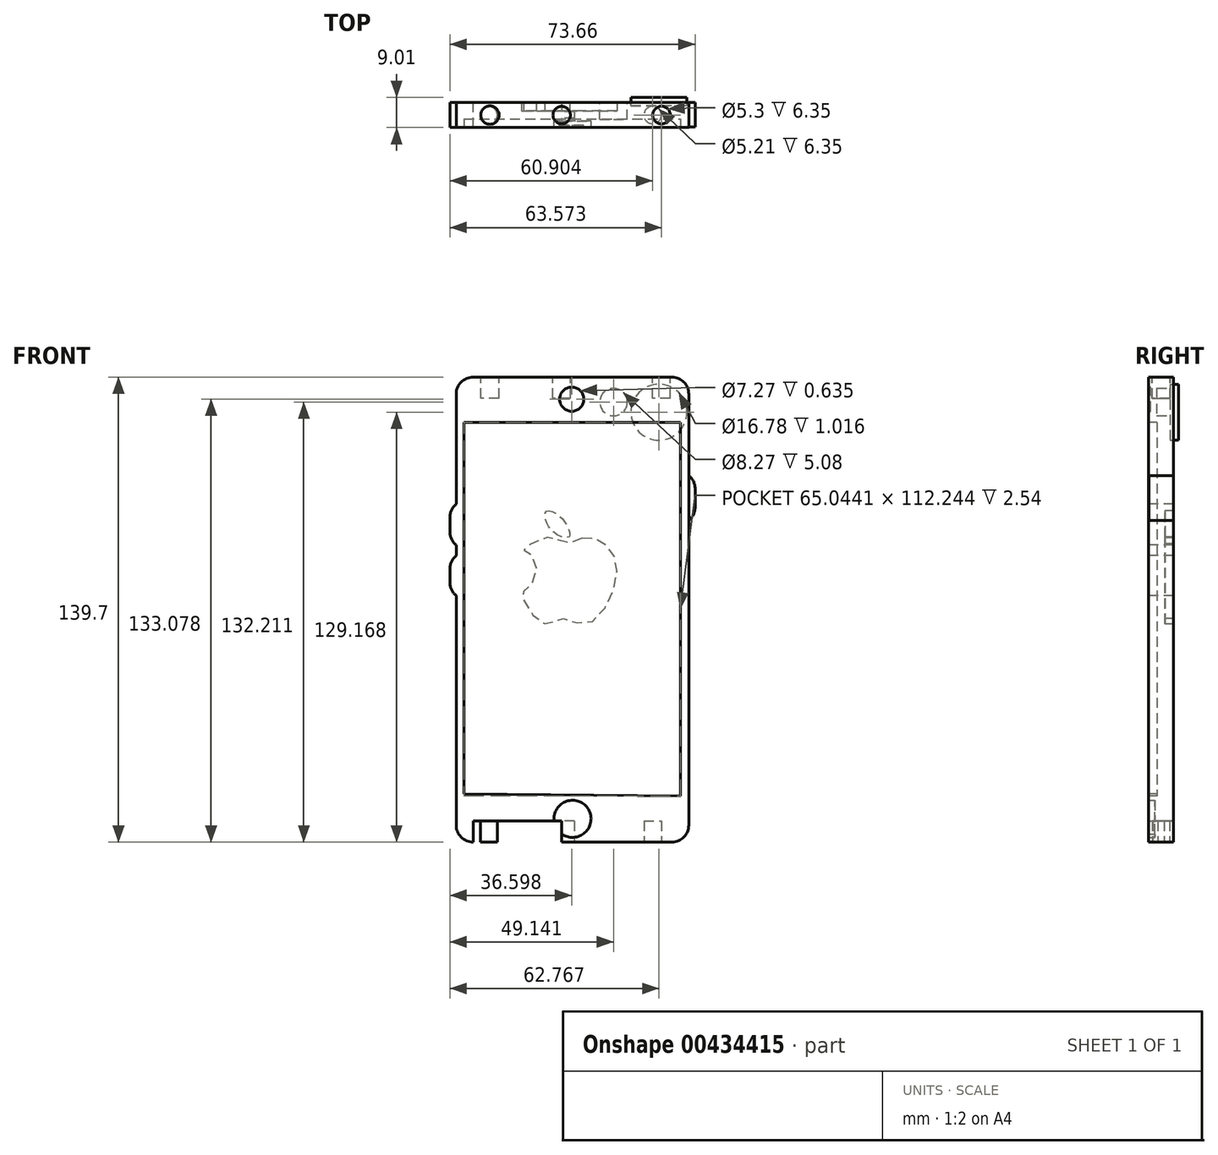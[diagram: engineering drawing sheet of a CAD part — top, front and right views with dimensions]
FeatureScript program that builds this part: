
annotation { "Feature Type Name" : "Feature", "Feature Type Description" : "" }
export const myFeature = defineFeature(function(context is Context, id is Id, definition is map)
    precondition{}
    {
        {
            var Q0;
            Q0=qCreatedBy(makeId("Front.planeOp"),FACE);
            var sketch = newSketch(context, id + "F0", { "sketchPlane" : qUnion([Q0])});
            skLineSegment(sketch, "E0.bottom", {"start": v(-31.68, 74.6) * mm, "end": v(38.17, 74.6) * mm});
            skLineSegment(sketch, "E0.top", {"start": v(-31.68, -65.1) * mm, "end": v(38.17, -65.1) * mm});
            skLineSegment(sketch, "E0.left", {"start": v(-31.68, 74.6) * mm, "end": v(-31.68, -65.1) * mm});
            skLineSegment(sketch, "E0.right", {"start": v(38.17, 74.6) * mm, "end": v(38.17, -65.1) * mm});
            skSolve(sketch);
        }
        {
            var Q0;
            Q0 = qSketchRegion(id + "F0", true);
            extrude(context, id + "F1", {"entities" : qUnion([Q0]), "depth" : 7.5 * mm});
        }
        {
            var Q0;
            Q0=makeQuery(id+"F1.opExtrude","SWEPT_EDGE",EDGE,{"disambiguationData":[OSD([sQuery(id+"F0.wireOp",EDGE,"E0.bottom"),sQuery(id+"F0.wireOp",EDGE,"E0.left")])]});
            var Q1;
            Q1=makeQuery(id+"F1.opExtrude","SWEPT_EDGE",EDGE,{"disambiguationData":[OSD([sQuery(id+"F0.wireOp",EDGE,"E0.bottom"),sQuery(id+"F0.wireOp",EDGE,"E0.right")])]});
            var Q2;
            Q2=makeQuery(id+"F1.opExtrude","SWEPT_EDGE",EDGE,{"disambiguationData":[OSD([sQuery(id+"F0.wireOp",EDGE,"E0.top"),sQuery(id+"F0.wireOp",EDGE,"E0.left")])]});
            var Q3;
            Q3=makeQuery(id+"F1.opExtrude","SWEPT_EDGE",EDGE,{"disambiguationData":[OSD([sQuery(id+"F0.wireOp",EDGE,"E0.top"),sQuery(id+"F0.wireOp",EDGE,"E0.right")])]});
            fillet(context, id + "F2", {"entities" : qUnion([Q0, Q1, Q2, Q3]), "radius" : 5.08 * mm, "tangentPropagation" : true, "allowEdgeOverflow" : false});
        }
        {
            var Q0;
            Q0=makeQuery(id+"F1.opExtrude","CAP_FACE",FACE,{"disambiguationData":[OSD([sQuery(id+"F0.wireOp",EDGE,"E0.bottom"),sQuery(id+"F0.wireOp",EDGE,"E0.top"),sQuery(id+"F0.wireOp",EDGE,"E0.left"),sQuery(id+"F0.wireOp",EDGE,"E0.right")])],"isStart":false});
            var sketch = newSketch(context, id + "F3", { "sketchPlane" : qUnion([Q0])});
            skLineSegment(sketch, "E1", {"start": v(-29.36, 61.01) * mm, "end": v(35.69, 61.01) * mm});
            skLineSegment(sketch, "E2", {"start": v(-29.36, 61.01) * mm, "end": v(-29.36, -50.65) * mm});
            skLineSegment(sketch, "E3", {"start": v(35.69, 61.01) * mm, "end": v(35.69, -51.23) * mm});
            skLineSegment(sketch, "E4", {"start": v(35.69, -51.23) * mm, "end": v(-29.36, -50.65) * mm});
            skSolve(sketch);
        }
        {
            var Q0;
            Q0 = qSketchRegion(id + "F3", true);
            extrude(context, id + "F4", {"entities" : qUnion([Q0]), "operationType" : NewBodyOperationType.REMOVE, "oppositeDirection" : true, "depth" : 2.54 * mm});
        }
        {
            var Q0;
            Q0=makeQuery(id+"F4.boolean.opBoolean","COPY",FACE,{"derivedFrom":makeQuery(id+"F4.opExtrude","CAP_FACE",FACE,{"disambiguationData":[OSD([sQuery(id+"F3.wireOp",EDGE,"E1"),sQuery(id+"F3.wireOp",EDGE,"E2"),sQuery(id+"F3.wireOp",EDGE,"E3"),sQuery(id+"F3.wireOp",EDGE,"E4")])],"isStart":false})});
            var sketch = newSketch(context, id + "F5", { "sketchPlane" : qUnion([Q0])});
            skSolve(sketch);
        }
        {
            var Q0;
            Q0 = qSketchRegion(id + "F5", true);
            var Q1;
            Q1=makeQuery(id+"F5.imprint","IMPRINT",FACE,{"disambiguationData":[TD([[makeQuery(id+"F5.imprint","IMPRINT",EDGE,{"derivedFrom":makeQuery(id+"F4.boolean.opBoolean","COPY",EDGE,{"derivedFrom":makeQuery(id+"F4.opExtrude","CAP_EDGE",EDGE,{"disambiguationData":[OSD([sQuery(id+"F3.wireOp",EDGE,"E1")])],"isStart":false})})}),-1.0]])]});
            extrude(context, id + "F6", {"entities" : qUnion([Q0, Q1]), "depth" : 2.54 * mm});
        }
        {
            var Q0;
            Q0=makeQuery(id+"F1.opExtrude","CAP_FACE",FACE,{"disambiguationData":[OSD([sQuery(id+"F0.wireOp",EDGE,"E0.bottom"),sQuery(id+"F0.wireOp",EDGE,"E0.top"),sQuery(id+"F0.wireOp",EDGE,"E0.left"),sQuery(id+"F0.wireOp",EDGE,"E0.right")])],"isStart":false});
            var sketch = newSketch(context, id + "F7", { "sketchPlane" : qUnion([Q0])});
            skCircle(sketch, "E5", {"center": v(3.24, -58.12) * mm, "radius": 5.57 * mm});
            skSolve(sketch);
        }
        {
            var Q0;
            Q0 = qSketchRegion(id + "F7", true);
            extrude(context, id + "F8", {"entities" : qUnion([Q0]), "operationType" : NewBodyOperationType.REMOVE, "oppositeDirection" : true, "depth" : 1.9 * mm});
        }
        {
            var Q0;
            Q0=makeQuery(id+"F8.boolean.opBoolean","COPY",FACE,{"derivedFrom":makeQuery(id+"F8.opExtrude","CAP_FACE",FACE,{"disambiguationData":[OSD([sQuery(id+"F7.wireOp",EDGE,"E5")])],"isStart":false})});
            var sketch = newSketch(context, id + "F9", { "sketchPlane" : qUnion([Q0])});
            skSolve(sketch);
        }
        {
            var Q0;
            Q0 = qSketchRegion(id + "F9", true);
            var Q1;
            Q1=makeQuery(id+"F9.imprint","IMPRINT",FACE,{"disambiguationData":[TD([[makeQuery(id+"F9.imprint","IMPRINT",EDGE,{"derivedFrom":makeQuery(id+"F8.boolean.opBoolean","COPY",EDGE,{"derivedFrom":makeQuery(id+"F8.opExtrude","CAP_EDGE",EDGE,{"disambiguationData":[OSD([sQuery(id+"F7.wireOp",EDGE,"E5")])],"isStart":false})})}),1.0]])]});
            extrude(context, id + "F10", {"entities" : qUnion([Q0, Q1]), "depth" : 1.9 * mm});
        }
        {
            var Q0;
            Q0=makeQuery(id+"F1.opExtrude","SWEPT_FACE",FACE,{"disambiguationData":[OSD([sQuery(id+"F0.wireOp",EDGE,"E0.bottom")])]});
            var sketch = newSketch(context, id + "F11", { "sketchPlane" : qUnion([Q0])});
            skCircle(sketch, "E6", {"center": v(0, -3.75) * mm, "radius": 2.63 * mm});
            skCircle(sketch, "E7", {"center": v(-21.56, -3.75) * mm, "radius": 2.75 * mm});
            skCircle(sketch, "E8", {"center": v(29.98, -3.75) * mm, "radius": 2.65 * mm});
            skPoint(sketch, "E9.orphan", {"position": v(-26.6, -3.75) * mm});
            skPoint(sketch, "E10.trimOffspring.end.orphan", {"position": v(33.09, -3.75) * mm});
            skPoint(sketch, "E11.orphan", {"position": v(0, -7.5) * mm});
            skPoint(sketch, "E12.start.orphan", {"position": v(0, 0) * mm});
            skSolve(sketch);
        }
        {
            var Q0;
            Q0 = qSketchRegion(id + "F11", true);
            extrude(context, id + "F12", {"entities" : qUnion([Q0]), "operationType" : NewBodyOperationType.REMOVE, "oppositeDirection" : true, "depth" : 6.35 * mm});
        }
        {
            var Q0;
            Q0=makeQuery(id+"F1.opExtrude","SWEPT_FACE",FACE,{"disambiguationData":[OSD([sQuery(id+"F0.wireOp",EDGE,"E0.top")])]});
            var sketch = newSketch(context, id + "F13", { "sketchPlane" : qUnion([Q0])});
            skLineSegment(sketch, "E13", {"start": v(0, 0) * mm, "end": v(0, 2.8) * mm});
            skLineSegment(sketch, "E14", {"start": v(-26.6, 3.75) * mm, "end": v(-3.81, 3.75) * mm});
            skLineSegment(sketch, "E15.bottom", {"start": v(3.81, 2.8) * mm, "end": v(-3.81, 2.8) * mm});
            skLineSegment(sketch, "E15.top", {"start": v(3.81, 4.7) * mm, "end": v(-3.81, 4.7) * mm});
            skLineSegment(sketch, "E15.left", {"start": v(3.8, 2.8) * mm, "end": v(3.8, 4.7) * mm});
            skLineSegment(sketch, "E15.right", {"start": v(-3.81, 2.8) * mm, "end": v(-3.81, 4.7) * mm});
            skPoint(sketch, "E15.middle", {"position": v(0, 3.75) * mm});
            skLineSegment(sketch, "E16.trimOffspring", {"start": v(3.81, 3.75) * mm, "end": v(33.09, 3.75) * mm});
            skLineSegment(sketch, "E17.trimOffspring", {"start": v(0, 4.7) * mm, "end": v(0, 7.5) * mm});
            skCircle(sketch, "E18", {"center": v(27.31, 3.75) * mm, "radius": 2.6 * mm});
            skCircle(sketch, "E19", {"center": v(-21.9, 3.75) * mm, "radius": 2.54 * mm});
            skSolve(sketch);
        }
        {
            var Q0;
            {var subQ6=sQuery(id+"F13.wireOp",EDGE,"E15.bottom");var subQ7=makeQuery(id+"F13.imprint","INTERSECT",VERTEX,{"derivedFrom":[sQuery(id+"F13.wireOp",EDGE,"E13"),subQ6]});Q0=makeQuery(id+"F13.imprint","IMPRINT",FACE,{"disambiguationData":[TD([[makeQuery(id+"F13.imprint","IMPRINT",EDGE,{"disambiguationData":[TD([[subQ7,1.0]])],"derivedFrom":subQ6}),-1.0]])]});}
            var Q1;
            {var subQ0=sQuery(id+"F13.wireOp",EDGE,"E19");var subQ1=sQuery(id+"F13.wireOp",EDGE,"E14");var subQ2=makeQuery(id+"F13.imprint","INTERSECT",VERTEX,{"disambiguationData":[OD(0.0)],"derivedFrom":[subQ1,subQ0]});Q1=makeQuery(id+"F13.imprint","IMPRINT",FACE,{"disambiguationData":[TD([[makeQuery(id+"F13.imprint","IMPRINT",EDGE,{"disambiguationData":[TD([[subQ2,-1.0]])],"derivedFrom":subQ1}),-1.0]])]});}
            var Q2;
            {var subQ0=sQuery(id+"F13.wireOp",EDGE,"E18");var subQ1=sQuery(id+"F13.wireOp",EDGE,"E16.trimOffspring");var subQ2=makeQuery(id+"F13.imprint","INTERSECT",VERTEX,{"disambiguationData":[OD(0.0)],"derivedFrom":[subQ1,subQ0]});Q2=makeQuery(id+"F13.imprint","IMPRINT",FACE,{"disambiguationData":[TD([[makeQuery(id+"F13.imprint","IMPRINT",EDGE,{"disambiguationData":[TD([[subQ2,-1.0]])],"derivedFrom":subQ1}),-1.0]])]});}
            var Q3;
            {var subQ0=sQuery(id+"F13.wireOp",EDGE,"E18");var subQ1=sQuery(id+"F13.wireOp",EDGE,"E16.trimOffspring");var subQ2=makeQuery(id+"F13.imprint","INTERSECT",VERTEX,{"disambiguationData":[OD(0.0)],"derivedFrom":[subQ1,subQ0]});Q3=makeQuery(id+"F13.imprint","IMPRINT",FACE,{"disambiguationData":[TD([[makeQuery(id+"F13.imprint","IMPRINT",EDGE,{"disambiguationData":[TD([[subQ2,-1.0]])],"derivedFrom":subQ1}),1.0]])]});}
            var Q4;
            {var subQ0=sQuery(id+"F13.wireOp",EDGE,"E19");var subQ1=sQuery(id+"F13.wireOp",EDGE,"E14");var subQ2=makeQuery(id+"F13.imprint","INTERSECT",VERTEX,{"disambiguationData":[OD(0.0)],"derivedFrom":[subQ1,subQ0]});Q4=makeQuery(id+"F13.imprint","IMPRINT",FACE,{"disambiguationData":[TD([[makeQuery(id+"F13.imprint","IMPRINT",EDGE,{"disambiguationData":[TD([[subQ2,-1.0]])],"derivedFrom":subQ1}),1.0]])]});}
            extrude(context, id + "F14", {"entities" : qUnion([Q0, Q1, Q2, Q3, Q4]), "operationType" : NewBodyOperationType.REMOVE, "oppositeDirection" : true, "depth" : 6.35 * mm});
        }
        {
            var Q0;
            Q0=makeQuery(id+"F1.opExtrude","CAP_FACE",FACE,{"disambiguationData":[OSD([sQuery(id+"F0.wireOp",EDGE,"E0.bottom"),sQuery(id+"F0.wireOp",EDGE,"E0.top"),sQuery(id+"F0.wireOp",EDGE,"E0.left"),sQuery(id+"F0.wireOp",EDGE,"E0.right")])],"isStart":false});
            var sketch = newSketch(context, id + "F15", { "sketchPlane" : qUnion([Q0])});
            skCircle(sketch, "E20", {"center": v(3, 67.98) * mm, "radius": 3.63 * mm});
            skSolve(sketch);
        }
        {
            var Q0;
            Q0 = qSketchRegion(id + "F15", true);
            extrude(context, id + "F16", {"entities" : qUnion([Q0]), "operationType" : NewBodyOperationType.REMOVE, "oppositeDirection" : true, "depth" : 0.64 * mm});
        }
        {
            var Q0;
            Q0=makeQuery(id+"F16.boolean.opBoolean","COPY",FACE,{"derivedFrom":makeQuery(id+"F16.opExtrude","CAP_FACE",FACE,{"disambiguationData":[OSD([sQuery(id+"F15.wireOp",EDGE,"E20")])],"isStart":false})});
            var sketch = newSketch(context, id + "F17", { "sketchPlane" : qUnion([Q0])});
            skSolve(sketch);
        }
        {
            var Q0;
            Q0 = qSketchRegion(id + "F17", true);
            var Q1;
            Q1=makeQuery(id+"F17.imprint","IMPRINT",FACE,{"disambiguationData":[TD([[makeQuery(id+"F17.imprint","IMPRINT",EDGE,{"derivedFrom":makeQuery(id+"F16.boolean.opBoolean","COPY",EDGE,{"derivedFrom":makeQuery(id+"F16.opExtrude","CAP_EDGE",EDGE,{"disambiguationData":[OSD([sQuery(id+"F15.wireOp",EDGE,"E20")])],"isStart":false})})}),1.0]])]});
            extrude(context, id + "F18", {"entities" : qUnion([Q0, Q1]), "depth" : 0.64 * mm});
        }
        {
            var Q0;
            Q0=makeQuery(id+"F1.opExtrude","SWEPT_FACE",FACE,{"disambiguationData":[OSD([sQuery(id+"F0.wireOp",EDGE,"E0.right")])]});
            var sketch = newSketch(context, id + "F19", { "sketchPlane" : qUnion([Q0])});
            skLineSegment(sketch, "E21.bottom", {"start": v(0, 31.58) * mm, "end": v(-7.37, 31.58) * mm});
            skLineSegment(sketch, "E21.top", {"start": v(0, 45.04) * mm, "end": v(-7.37, 45.04) * mm});
            skLineSegment(sketch, "E21.left", {"start": v(0, 31.58) * mm, "end": v(0, 45.04) * mm});
            skLineSegment(sketch, "E21.right", {"start": v(-7.37, 31.58) * mm, "end": v(-7.37, 45.04) * mm});
            skPoint(sketch, "E21.middle", {"position": v(-3.68, 38.31) * mm});
            skSolve(sketch);
        }
        {
            var Q0;
            Q0 = qSketchRegion(id + "F19", true);
            extrude(context, id + "F20", {"entities" : qUnion([Q0]), "operationType" : NewBodyOperationType.ADD, "depth" : 1.9 * mm});
        }
        {
            var Q0;
            Q0=makeQuery(id+"F20.opExtrude","CAP_EDGE",EDGE,{"disambiguationData":[OSD([sQuery(id+"F19.wireOp",EDGE,"E21.top")])],"isStart":false});
            var Q1;
            Q1=makeQuery(id+"F20.opExtrude","CAP_EDGE",EDGE,{"disambiguationData":[OSD([sQuery(id+"F19.wireOp",EDGE,"E21.bottom")])],"isStart":false});
            fillet(context, id + "F21", {"entities" : qUnion([Q0, Q1]), "radius" : 5.08 * mm, "tangentPropagation" : true, "allowEdgeOverflow" : false});
        }
        {
            var Q0;
            Q0=makeQuery(id+"F20.boolean.opBoolean","MERGE",FACE,{"derivedFrom":[makeQuery(id+"F1.opExtrude","CAP_FACE",FACE,{"disambiguationData":[OSD([sQuery(id+"F0.wireOp",EDGE,"E0.bottom"),sQuery(id+"F0.wireOp",EDGE,"E0.top"),sQuery(id+"F0.wireOp",EDGE,"E0.left"),sQuery(id+"F0.wireOp",EDGE,"E0.right")])],"isStart":true}),makeQuery(id+"F20.opExtrude","SWEPT_FACE",FACE,{"disambiguationData":[OSD([sQuery(id+"F19.wireOp",EDGE,"E21.left")])]})]});
            var sketch = newSketch(context, id + "F22", { "sketchPlane" : qUnion([Q0])});
            skCircle(sketch, "E22", {"center": v(-29.18, 64.07) * mm, "radius": 8.39 * mm});
            skSolve(sketch);
        }
        {
            var Q0;
            Q0 = qSketchRegion(id + "F22", true);
            extrude(context, id + "F23", {"entities" : qUnion([Q0]), "operationType" : NewBodyOperationType.REMOVE, "oppositeDirection" : true, "depth" : 1.02 * mm});
        }
        {
            var Q0;
            Q0=makeQuery(id+"F23.boolean.opBoolean","COPY",FACE,{"derivedFrom":makeQuery(id+"F23.opExtrude","CAP_FACE",FACE,{"disambiguationData":[OSD([sQuery(id+"F22.wireOp",EDGE,"E22")])],"isStart":false})});
            var sketch = newSketch(context, id + "F24", { "sketchPlane" : qUnion([Q0])});
            skSolve(sketch);
        }
        {
            var Q0;
            Q0=makeQuery(id+"F24.imprint","IMPRINT",FACE,{"disambiguationData":[TD([[makeQuery(id+"F24.imprint","IMPRINT",EDGE,{"derivedFrom":makeQuery(id+"F23.boolean.opBoolean","COPY",EDGE,{"derivedFrom":makeQuery(id+"F23.opExtrude","CAP_EDGE",EDGE,{"disambiguationData":[OSD([sQuery(id+"F22.wireOp",EDGE,"E22")])],"isStart":false})})}),1.0]])]});
            extrude(context, id + "F25", {"entities" : qUnion([Q0]), "depth" : 2.54 * mm});
        }
        {
            var Q0;
            Q0=makeQuery(id+"F20.boolean.opBoolean","MERGE",FACE,{"derivedFrom":[makeQuery(id+"F1.opExtrude","CAP_FACE",FACE,{"disambiguationData":[OSD([sQuery(id+"F0.wireOp",EDGE,"E0.bottom"),sQuery(id+"F0.wireOp",EDGE,"E0.top"),sQuery(id+"F0.wireOp",EDGE,"E0.left"),sQuery(id+"F0.wireOp",EDGE,"E0.right")])],"isStart":true}),makeQuery(id+"F20.opExtrude","SWEPT_FACE",FACE,{"disambiguationData":[OSD([sQuery(id+"F19.wireOp",EDGE,"E21.left")])]})]});
            var sketch = newSketch(context, id + "F26", { "sketchPlane" : qUnion([Q0])});
            skCircle(sketch, "E23", {"center": v(-15.55, 67.11) * mm, "radius": 4.13 * mm});
            skSolve(sketch);
        }
        {
            var Q0;
            Q0 = qSketchRegion(id + "F26", true);
            extrude(context, id + "F27", {"entities" : qUnion([Q0]), "operationType" : NewBodyOperationType.REMOVE, "oppositeDirection" : true, "depth" : 5.08 * mm});
        }
        {
            var Q0;
            Q0=makeQuery(id+"F27.boolean.opBoolean","COPY",FACE,{"derivedFrom":makeQuery(id+"F27.opExtrude","CAP_FACE",FACE,{"disambiguationData":[OSD([sQuery(id+"F26.wireOp",EDGE,"E23")])],"isStart":false})});
            var sketch = newSketch(context, id + "F28", { "sketchPlane" : qUnion([Q0])});
            skSolve(sketch);
        }
        {
            var Q0;
            Q0 = qSketchRegion(id + "F28", true);
            var Q1;
            Q1=makeQuery(id+"F28.imprint","IMPRINT",FACE,{"disambiguationData":[TD([[makeQuery(id+"F28.imprint","IMPRINT",EDGE,{"derivedFrom":makeQuery(id+"F27.boolean.opBoolean","COPY",EDGE,{"derivedFrom":makeQuery(id+"F27.opExtrude","CAP_EDGE",EDGE,{"disambiguationData":[OSD([sQuery(id+"F26.wireOp",EDGE,"E23")])],"isStart":false})})}),1.0]])]});
            extrude(context, id + "F29", {"entities" : qUnion([Q0, Q1]), "depth" : 5.08 * mm});
        }
        {
            var Q0;
            Q0=makeQuery(id+"F20.boolean.opBoolean","MERGE",FACE,{"derivedFrom":[makeQuery(id+"F1.opExtrude","CAP_FACE",FACE,{"disambiguationData":[OSD([sQuery(id+"F0.wireOp",EDGE,"E0.bottom"),sQuery(id+"F0.wireOp",EDGE,"E0.top"),sQuery(id+"F0.wireOp",EDGE,"E0.left"),sQuery(id+"F0.wireOp",EDGE,"E0.right")])],"isStart":true}),makeQuery(id+"F20.opExtrude","SWEPT_FACE",FACE,{"disambiguationData":[OSD([sQuery(id+"F19.wireOp",EDGE,"E21.left")])]})]});
            var sketch = newSketch(context, id + "F30", { "sketchPlane" : qUnion([Q0])});
            skFitSpline(sketch, "E24", {"points": [v(-6.1, 26.14) * mm, v(-1.6, 24.63) * mm, v(3.79, 26.54) * mm, v(11.48, 22.77) * mm, v(10.53, 22.5) * mm, v(7.66, 17.55) * mm, v(10.59, 10.58) * mm, v(12.05, 9.68) * mm, v(7.05, 1.53) * mm, v(3.17, 0.74) * mm, v(0, 2.1) * mm, v(-7.45, 0.52) * mm, v(-15.32, 10.02) * mm, v(-16, 20.24) * mm, v(-11.73, 25.3) * mm, v(-6.1, 26.14) * mm]});
            skFitSpline(sketch, "E25", {"points": [v(4.58, 34.28) * mm, v(0.67, 32.92) * mm, v(-2.35, 27.89) * mm, v(-2.11, 26.54) * mm, v(1.38, 27.24) * mm, v(4.75, 31.44) * mm, v(4.58, 34.28) * mm]});
            skSolve(sketch);
        }
        {
            var Q0;
            Q0=makeQuery(id+"F30.imprint","IMPRINT",FACE,{"disambiguationData":[TD([[makeQuery(id+"F30.imprint","IMPRINT",EDGE,{"derivedFrom":sQuery(id+"F30.wireOp",EDGE,"E25")}),1.0]])]});
            var sketch = newSketch(context, id + "F31", { "sketchPlane" : qUnion([Q0])});
            skSolve(sketch);
        }
        {
            var Q0;
            Q0=makeQuery(id+"F30.imprint","IMPRINT",FACE,{"disambiguationData":[TD([[makeQuery(id+"F30.imprint","IMPRINT",EDGE,{"derivedFrom":sQuery(id+"F30.wireOp",EDGE,"E24")}),-1.0]])]});
            extrude(context, id + "F32", {"entities" : qUnion([Q0]), "operationType" : NewBodyOperationType.REMOVE, "oppositeDirection" : true, "depth" : 2.54 * mm});
        }
        {
            var Q0;
            Q0=makeQuery(id+"F31.imprint","IMPRINT",FACE,{"disambiguationData":[TD([[makeQuery(id+"F31.imprint","IMPRINT",EDGE,{"derivedFrom":makeQuery(id+"F30.imprint","IMPRINT",EDGE,{"derivedFrom":sQuery(id+"F30.wireOp",EDGE,"E25")})}),1.0]])]});
            extrude(context, id + "F33", {"entities" : qUnion([Q0]), "operationType" : NewBodyOperationType.REMOVE, "oppositeDirection" : true, "depth" : 2.54 * mm});
        }
        {
            var Q0;
            Q0=makeQuery(id+"F33.boolean.opBoolean","COPY",FACE,{"derivedFrom":makeQuery(id+"F33.opExtrude","CAP_FACE",FACE,{"disambiguationData":[OSD([sQuery(id+"F30.wireOp",EDGE,"E25")])],"isStart":false})});
            var sketch = newSketch(context, id + "F34", { "sketchPlane" : qUnion([Q0])});
            skSolve(sketch);
        }
        {
            var Q0;
            Q0 = qSketchRegion(id + "F34", true);
            var Q1;
            Q1=makeQuery(id+"F34.imprint","IMPRINT",FACE,{"disambiguationData":[TD([[makeQuery(id+"F34.imprint","IMPRINT",EDGE,{"derivedFrom":makeQuery(id+"F33.boolean.opBoolean","COPY",EDGE,{"derivedFrom":makeQuery(id+"F33.opExtrude","CAP_EDGE",EDGE,{"disambiguationData":[OSD([sQuery(id+"F30.wireOp",EDGE,"E25")])],"isStart":false})})}),1.0]])]});
            extrude(context, id + "F35", {"entities" : qUnion([Q0, Q1]), "depth" : 2.54 * mm});
        }
        {
            var Q0;
            Q0=makeQuery(id+"F32.boolean.opBoolean","COPY",FACE,{"derivedFrom":makeQuery(id+"F32.opExtrude","CAP_FACE",FACE,{"disambiguationData":[OSD([sQuery(id+"F30.wireOp",EDGE,"E24")])],"isStart":false})});
            var sketch = newSketch(context, id + "F36", { "sketchPlane" : qUnion([Q0])});
            skSolve(sketch);
        }
        {
            var Q0;
            Q0=makeQuery(id+"F36.imprint","IMPRINT",FACE,{"disambiguationData":[TD([[makeQuery(id+"F36.imprint","IMPRINT",EDGE,{"derivedFrom":makeQuery(id+"F32.boolean.opBoolean","COPY",EDGE,{"derivedFrom":makeQuery(id+"F32.opExtrude","CAP_EDGE",EDGE,{"disambiguationData":[OSD([sQuery(id+"F30.wireOp",EDGE,"E24")])],"isStart":false})})}),-1.0]])]});
            extrude(context, id + "F37", {"entities" : qUnion([Q0]), "depth" : 2.54 * mm});
        }
        {
            var Q0;
            Q0=makeQuery(id+"F1.opExtrude","SWEPT_FACE",FACE,{"disambiguationData":[OSD([sQuery(id+"F0.wireOp",EDGE,"E0.left")])]});
            var sketch = newSketch(context, id + "F38", { "sketchPlane" : qUnion([Q0])});
            skLineSegment(sketch, "E26.bottom", {"start": v(0, 36.44) * mm, "end": v(7.5, 36.44) * mm});
            skLineSegment(sketch, "E26.top", {"start": v(0, 24.12) * mm, "end": v(7.5, 24.12) * mm});
            skLineSegment(sketch, "E26.left", {"start": v(0, 36.44) * mm, "end": v(0, 24.12) * mm});
            skLineSegment(sketch, "E26.right", {"start": v(7.5, 36.44) * mm, "end": v(7.5, 24.12) * mm});
            skLineSegment(sketch, "E27.bottom", {"start": v(0, 20.95) * mm, "end": v(7.5, 20.95) * mm});
            skLineSegment(sketch, "E27.top", {"start": v(0, 8.94) * mm, "end": v(7.5, 8.94) * mm});
            skLineSegment(sketch, "E27.left", {"start": v(0, 20.95) * mm, "end": v(0, 8.94) * mm});
            skLineSegment(sketch, "E27.right", {"start": v(7.5, 20.95) * mm, "end": v(7.5, 8.94) * mm});
            skSolve(sketch);
        }
        {
            var Q0;
            Q0 = qSketchRegion(id + "F38", true);
            extrude(context, id + "F39", {"entities" : qUnion([Q0]), "operationType" : NewBodyOperationType.ADD, "depth" : 1.9 * mm});
        }
        {
            var Q0;
            Q0=makeQuery(id+"F39.opExtrude","CAP_EDGE",EDGE,{"disambiguationData":[OSD([sQuery(id+"F38.wireOp",EDGE,"E27.top")])],"isStart":false});
            var Q1;
            Q1=makeQuery(id+"F39.opExtrude","CAP_EDGE",EDGE,{"disambiguationData":[OSD([sQuery(id+"F38.wireOp",EDGE,"E26.bottom")])],"isStart":false});
            var Q2;
            Q2=makeQuery(id+"F39.opExtrude","CAP_EDGE",EDGE,{"disambiguationData":[OSD([sQuery(id+"F38.wireOp",EDGE,"E27.bottom")])],"isStart":false});
            var Q3;
            Q3=makeQuery(id+"F39.opExtrude","CAP_EDGE",EDGE,{"disambiguationData":[OSD([sQuery(id+"F38.wireOp",EDGE,"E26.top")])],"isStart":false});
            fillet(context, id + "F40", {"entities" : qUnion([Q0, Q1, Q2, Q3]), "radius" : 5.08 * mm, "tangentPropagation" : true, "allowEdgeOverflow" : false});
        }
    });
